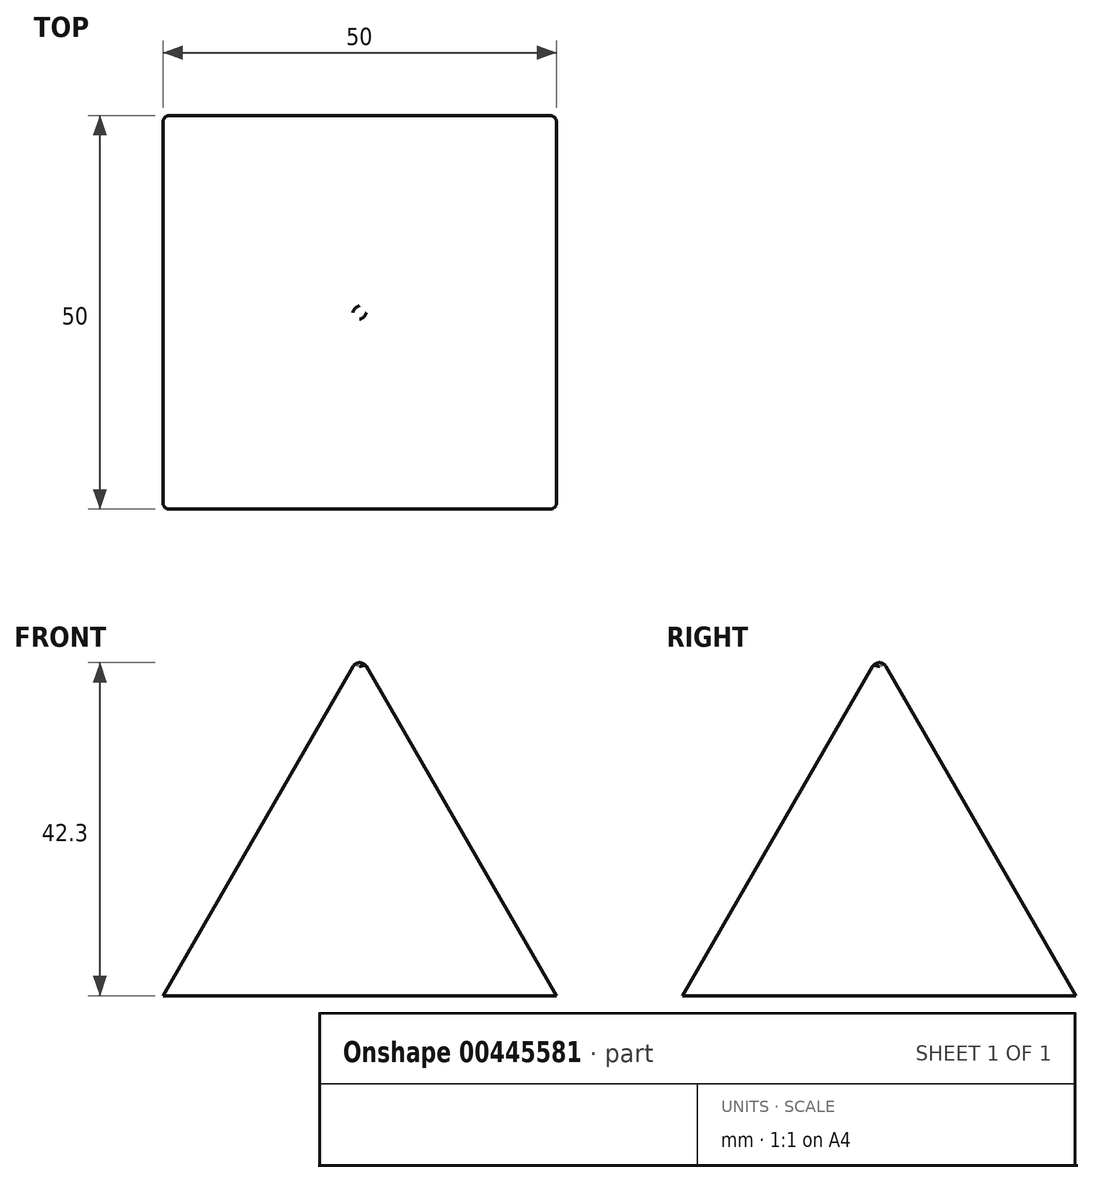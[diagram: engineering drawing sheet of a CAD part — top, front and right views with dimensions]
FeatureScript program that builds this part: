
annotation { "Feature Type Name" : "Feature", "Feature Type Description" : "" }
export const myFeature = defineFeature(function(context is Context, id is Id, definition is map)
    precondition{}
    {
        {
            var Q0;
            Q0=qCreatedBy(makeId("Top.planeOp"),FACE);
            var sketch = newSketch(context, id + "F0", { "sketchPlane" : qUnion([Q0])});
            skLineSegment(sketch, "E0.bottom", {"start": v(25, -25) * mm, "end": v(-25, -25) * mm});
            skLineSegment(sketch, "E0.top", {"start": v(25, 25) * mm, "end": v(-25, 25) * mm});
            skLineSegment(sketch, "E0.left", {"start": v(25, -25) * mm, "end": v(25, 25) * mm});
            skLineSegment(sketch, "E0.right", {"start": v(-25, -25) * mm, "end": v(-25, 25) * mm});
            skPoint(sketch, "E0.middle", {"position": v(0, 0) * mm});
            skSolve(sketch);
        }
        {
            var Q0;
            Q0=qSketchRegion(id+"F0",true);
            extrude(context, id + "F1", {"entities" : qUnion([Q0]), "depth" : 50 * mm, "hasDraft" : true, "draftAngle" : 30 * degree, "draftPullDirection" : true});
        }
        {
            var Q0;
            Q0=makeQuery(id+"F1.opExtrude","SWEPT_EDGE",EDGE,{"disambiguationData":[OSD([sQuery(id+"F0.wireOp",EDGE,"E0.bottom"),sQuery(id+"F0.wireOp",EDGE,"E0.right")])]});
            var Q1;
            Q1=makeQuery(id+"F1.opExtrude","SWEPT_EDGE",EDGE,{"disambiguationData":[OSD([sQuery(id+"F0.wireOp",EDGE,"E0.top"),sQuery(id+"F0.wireOp",EDGE,"E0.right")])]});
            var Q2;
            Q2=makeQuery(id+"F1.opExtrude","SWEPT_EDGE",EDGE,{"disambiguationData":[OSD([sQuery(id+"F0.wireOp",EDGE,"E0.top"),sQuery(id+"F0.wireOp",EDGE,"E0.left")])]});
            var Q3;
            Q3=makeQuery(id+"F1.opExtrude","SWEPT_EDGE",EDGE,{"disambiguationData":[OSD([sQuery(id+"F0.wireOp",EDGE,"E0.bottom"),sQuery(id+"F0.wireOp",EDGE,"E0.left")])]});
            fillet(context, id + "F2", {"entities" : qUnion([Q0, Q1, Q2, Q3]), "radius" : 1 * mm, "tangentPropagation" : true, "allowEdgeOverflow" : false});
        }
    });
